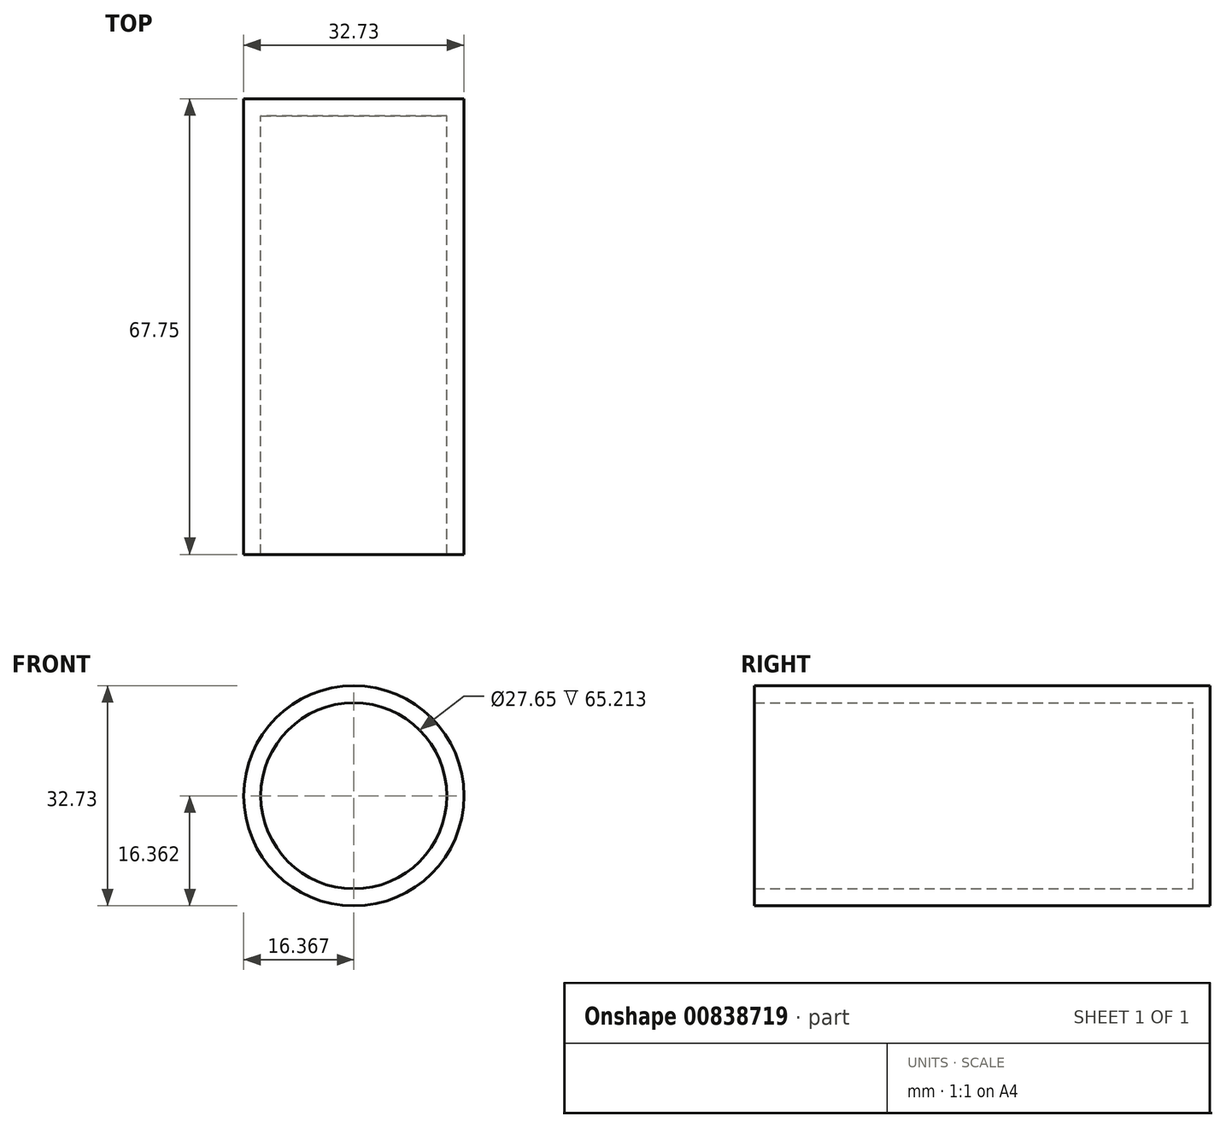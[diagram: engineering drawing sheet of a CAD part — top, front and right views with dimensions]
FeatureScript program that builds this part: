
annotation { "Feature Type Name" : "Feature", "Feature Type Description" : "" }
export const myFeature = defineFeature(function(context is Context, id is Id, definition is map)
    precondition{}
    {
        {
            var Q0;
            Q0=qCreatedBy(makeId("Front.planeOp"),FACE);
            var sketch = newSketch(context, id + "F0", { "sketchPlane" : qUnion([Q0])});
            skCircle(sketch, "E0", {"center": v(-0.66, -0.75) * mm, "radius": 16.37 * mm});
            skSolve(sketch);
        }
        {
            var Q0;
            Q0=makeQuery(id+"F0.imprint","IMPRINT",FACE,{"disambiguationData":[TD([[makeQuery(id+"F0.imprint","IMPRINT",EDGE,{"derivedFrom":sQuery(id+"F0.wireOp",EDGE,"E0")}),1.0]])]});
            var Q1;
            Q1=sQuery(id+"F0.wireOp",EDGE,"E0");
            extrude(context, id + "F1", {"entities" : qUnion([Q0]), "surfaceEntities" : qUnion([Q1]), "depth" : 67.75 * mm, "offsetDistance" : 25.4 * mm});
        }
        {
            var Q0;
            Q0=makeQuery(id+"F1.opExtrude","CAP_FACE",FACE,{"disambiguationData":[OSD([sQuery(id+"F0.wireOp",EDGE,"E0")])],"isStart":false});
            shell(context, id + "F2", {"entities" : qUnion([Q0]), "thickness" : 2.54 * mm});
        }
    });
